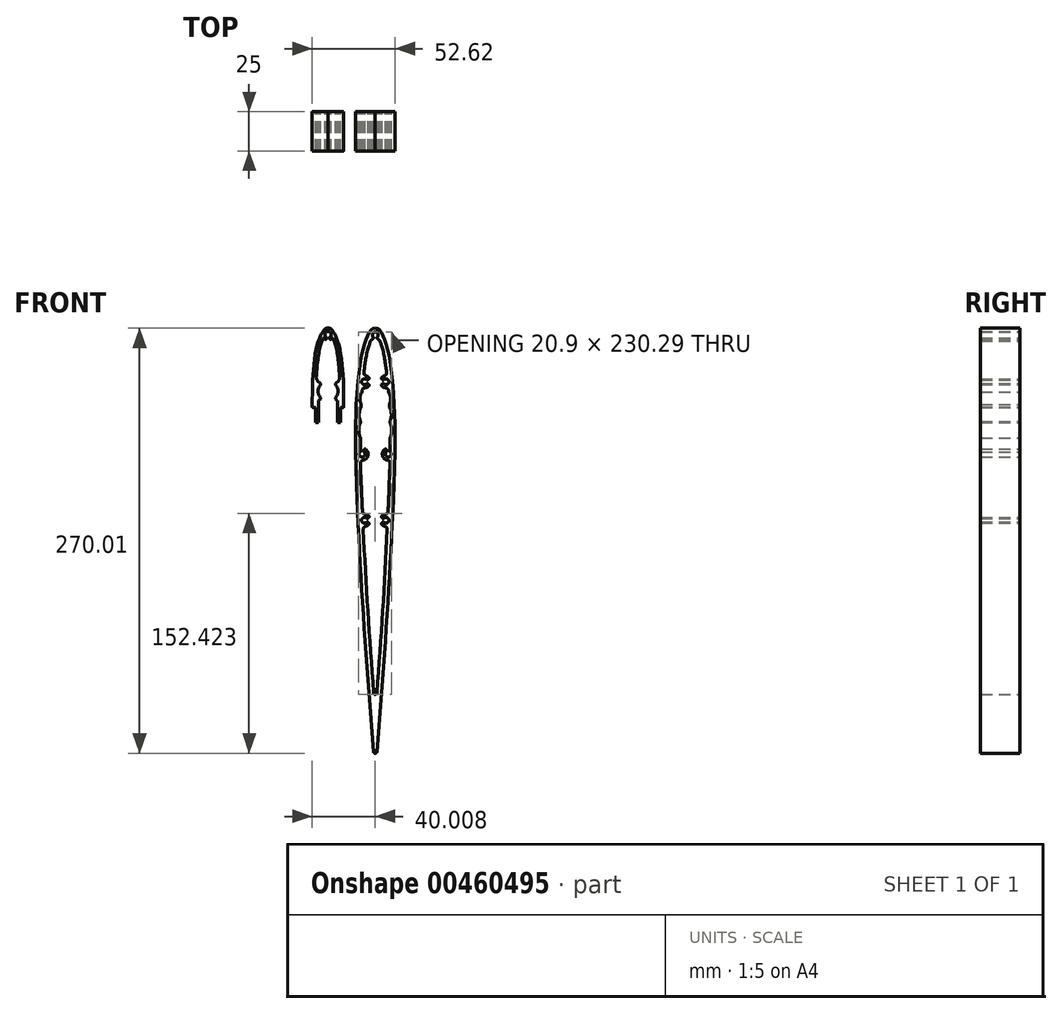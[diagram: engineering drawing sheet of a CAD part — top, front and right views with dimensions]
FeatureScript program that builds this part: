
annotation { "Feature Type Name" : "Feature", "Feature Type Description" : "" }
export const myFeature = defineFeature(function(context is Context, id is Id, definition is map)
    precondition{}
    {
        {
            var Q0;
            Q0=qCreatedBy(makeId("Front.planeOp"),FACE);
            var sketch = newSketch(context, id + "F0", { "sketchPlane" : qUnion([Q0])});
            skLineSegment(sketch, "E0", {"start": v(-26, 84.74) * mm, "end": v(-24.5, 84.74) * mm});
            skArc(sketch, "E1", {"start": v(-26.25, 85) * mm, "mid": v(-26.17, 84.82) * mm, "end": v(-26, 84.74) * mm});
            skFitSpline(sketch, "E2", {"points": [v(-26.25, 85) * mm, v(-26.24, 88.67) * mm, v(-26.08, 98.58) * mm, v(-25.1, 113) * mm, v(-22.87, 125.21) * mm, v(-20.9, 130.42) * mm, v(-19.33, 133.17) * mm, v(-17.9, 134.65) * mm, v(-16.79, 135) * mm, v(-16.24, 135) * mm]});
            skFitSpline(sketch, "E3", {"points": [v(-16.24, 135) * mm, v(-15.7, 135) * mm, v(-14.58, 134.65) * mm, v(-13.16, 133.17) * mm, v(-11.58, 130.42) * mm, v(-9.61, 125.21) * mm, v(-7.38, 113) * mm, v(-6.4, 98.58) * mm, v(-6.24, 88.67) * mm, v(-6.24, 85) * mm]});
            skArc(sketch, "E4", {"start": v(-6.49, 84.74) * mm, "mid": v(-6.3, 84.82) * mm, "end": v(-6.24, 85) * mm});
            skLineSegment(sketch, "E5", {"start": v(-7.99, 84.74) * mm, "end": v(-6.49, 84.74) * mm});
            skArc(sketch, "E6", {"start": v(-7.99, 84.74) * mm, "mid": v(-8.16, 84.67) * mm, "end": v(-8.24, 84.5) * mm});
            skLineSegment(sketch, "E7", {"start": v(-8.24, 84.5) * mm, "end": v(-8.24, 75) * mm});
            skArc(sketch, "E8", {"start": v(-10.24, 88.79) * mm, "mid": v(-10.27, 88.98) * mm, "end": v(-10.38, 89.14) * mm});
            skLineSegment(sketch, "E9", {"start": v(-11.41, 90.17) * mm, "end": v(-10.38, 89.14) * mm});
            skArc(sketch, "E10", {"start": v(-11.44, 90.85) * mm, "mid": v(-11.56, 90.5) * mm, "end": v(-11.41, 90.17) * mm});
            skArc(sketch, "E11", {"start": v(-11.44, 90.85) * mm, "mid": v(-9.9, 95) * mm, "end": v(-11.44, 99.15) * mm});
            skArc(sketch, "E12", {"start": v(-11.41, 99.83) * mm, "mid": v(-11.56, 99.5) * mm, "end": v(-11.44, 99.15) * mm});
            skLineSegment(sketch, "E13", {"start": v(-11.41, 99.83) * mm, "end": v(-9.68, 101.56) * mm});
            skArc(sketch, "E14", {"start": v(-9.68, 101.56) * mm, "mid": v(-9, 102.63) * mm, "end": v(-8.81, 103.89) * mm});
            skFitSpline(sketch, "E15", {"points": [v(-8.81, 103.89) * mm, v(-8.97, 106.15) * mm, v(-9.72, 114.71) * mm, v(-11.32, 123.38) * mm, v(-12.63, 127.4) * mm, v(-12.98, 128.32) * mm]});
            skArc(sketch, "E16", {"start": v(-12.98, 128.32) * mm, "mid": v(-13.34, 128.63) * mm, "end": v(-13.8, 128.5) * mm});
            skArc(sketch, "E17", {"start": v(-14.5, 127.97) * mm, "mid": v(-14.13, 128.21) * mm, "end": v(-13.8, 128.5) * mm});
            skArc(sketch, "E18", {"start": v(-15.24, 128.4) * mm, "mid": v(-15, 127.97) * mm, "end": v(-14.5, 127.97) * mm});
            skLineSegment(sketch, "E19", {"start": v(-15.24, 129) * mm, "end": v(-15.24, 128.4) * mm});
            skArc(sketch, "E20", {"start": v(-15.04, 129.4) * mm, "mid": v(-15.19, 129.22) * mm, "end": v(-15.24, 129) * mm});
            skArc(sketch, "E21", {"start": v(-15.04, 129.4) * mm, "mid": v(-16.24, 133) * mm, "end": v(-17.44, 129.4) * mm});
            skArc(sketch, "E22", {"start": v(-17.24, 129) * mm, "mid": v(-17.3, 129.22) * mm, "end": v(-17.44, 129.4) * mm});
            skLineSegment(sketch, "E23", {"start": v(-17.24, 128.4) * mm, "end": v(-17.24, 129) * mm});
            skArc(sketch, "E24", {"start": v(-18, 127.97) * mm, "mid": v(-17.5, 127.97) * mm, "end": v(-17.24, 128.4) * mm});
            skArc(sketch, "E25", {"start": v(-18.69, 128.5) * mm, "mid": v(-18.36, 128.21) * mm, "end": v(-18, 127.97) * mm});
            skArc(sketch, "E26", {"start": v(-18.69, 128.5) * mm, "mid": v(-19.15, 128.63) * mm, "end": v(-19.5, 128.32) * mm});
            skFitSpline(sketch, "E27", {"points": [v(-19.5, 128.32) * mm, v(-19.86, 127.4) * mm, v(-21.16, 123.38) * mm, v(-22.76, 114.71) * mm, v(-23.52, 106.15) * mm, v(-23.67, 103.89) * mm]});
            skArc(sketch, "E28", {"start": v(-23.67, 103.89) * mm, "mid": v(-23.49, 102.63) * mm, "end": v(-22.8, 101.56) * mm});
            skLineSegment(sketch, "E29", {"start": v(-22.8, 101.56) * mm, "end": v(-21.07, 99.83) * mm});
            skArc(sketch, "E30", {"start": v(-21.05, 99.15) * mm, "mid": v(-20.93, 99.5) * mm, "end": v(-21.07, 99.83) * mm});
            skArc(sketch, "E31", {"start": v(-21.05, 99.15) * mm, "mid": v(-22.6, 95) * mm, "end": v(-21.05, 90.85) * mm});
            skArc(sketch, "E32", {"start": v(-21.07, 90.17) * mm, "mid": v(-20.93, 90.5) * mm, "end": v(-21.05, 90.85) * mm});
            skLineSegment(sketch, "E33", {"start": v(-22.1, 89.14) * mm, "end": v(-21.07, 90.17) * mm});
            skArc(sketch, "E34", {"start": v(-22.1, 89.14) * mm, "mid": v(-22.2, 88.98) * mm, "end": v(-22.25, 88.79) * mm});
            skLineSegment(sketch, "E35", {"start": v(-24.25, 75) * mm, "end": v(-24.25, 84.5) * mm});
            skArc(sketch, "E36", {"start": v(-24.25, 84.5) * mm, "mid": v(-24.32, 84.67) * mm, "end": v(-24.5, 84.74) * mm});
            skLineSegment(sketch, "E37", {"start": v(-8.24, 75) * mm, "end": v(-10.24, 75) * mm});
            skLineSegment(sketch, "E38", {"start": v(-22.25, 88.79) * mm, "end": v(-22.25, 75) * mm});
            skLineSegment(sketch, "E39", {"start": v(-22.25, 75) * mm, "end": v(-24.25, 75) * mm});
            skLineSegment(sketch, "E40", {"start": v(-10.24, 75) * mm, "end": v(-10.24, 88.79) * mm});
            skArc(sketch, "E41", {"start": v(1.9, 35) * mm, "mid": v(5.19, -30.83) * mm, "end": v(9.73, -96.58) * mm});
            skFitSpline(sketch, "E42", {"points": [v(1.9, 35) * mm, v(1.67, 41.44) * mm, v(1.23, 54.34) * mm, v(1.24, 72.62) * mm, v(1.85, 89.82) * mm, v(2.95, 103.2) * mm, v(4.43, 113.85) * mm, v(5.71, 120.45) * mm, v(7.11, 125.63) * mm, v(8.23, 128.8) * mm, v(9.37, 131.23) * mm, v(10.3, 132.77) * mm, v(11.33, 133.95) * mm, v(12.42, 134.8) * mm, v(13.31, 134.93) * mm, v(13.76, 135) * mm]});
            skFitSpline(sketch, "E43", {"points": [v(25.63, 35) * mm, v(25.85, 41.44) * mm, v(26.29, 54.34) * mm, v(26.28, 72.62) * mm, v(25.66, 89.82) * mm, v(24.57, 103.2) * mm, v(23.09, 113.85) * mm, v(21.8, 120.45) * mm, v(20.4, 125.63) * mm, v(19.3, 128.8) * mm, v(18.15, 131.23) * mm, v(17.2, 132.77) * mm, v(16.18, 133.95) * mm, v(15.1, 134.8) * mm, v(14.2, 134.93) * mm, v(13.76, 135) * mm]});
            skArc(sketch, "E44", {"start": v(17.78, -96.58) * mm, "mid": v(22.33, -30.83) * mm, "end": v(25.63, 35) * mm});
            skLineSegment(sketch, "E45", {"start": v(14.84, -134) * mm, "end": v(17.78, -96.58) * mm});
            skLineSegment(sketch, "E46", {"start": v(12.68, -134) * mm, "end": v(9.73, -96.58) * mm});
            skArc(sketch, "E47", {"start": v(11.9, 127.93) * mm, "mid": v(12.51, 128.6) * mm, "end": v(12.32, 129.5) * mm});
            skArc(sketch, "E48", {"start": v(11.9, 127.93) * mm, "mid": v(11.17, 127.47) * mm, "end": v(10.7, 126.74) * mm});
            skFitSpline(sketch, "E49", {"points": [v(6.52, 106.91) * mm, v(6.59, 107.43) * mm, v(7.07, 111.18) * mm, v(8.03, 116.97) * mm, v(9.45, 123.07) * mm, v(10.41, 125.9) * mm, v(10.7, 126.74) * mm]});
            skArc(sketch, "E50", {"start": v(6.52, 106.91) * mm, "mid": v(6.84, 105.55) * mm, "end": v(7.98, 104.73) * mm});
            skArc(sketch, "E51", {"start": v(9.43, 103.98) * mm, "mid": v(8.75, 104.44) * mm, "end": v(7.98, 104.73) * mm});
            skArc(sketch, "E52", {"start": v(8.16, 102.44) * mm, "mid": v(9.56, 102.57) * mm, "end": v(9.43, 103.98) * mm});
            skArc(sketch, "E53", {"start": v(8.16, 102.44) * mm, "mid": v(5.1, 101) * mm, "end": v(8.16, 99.56) * mm});
            skArc(sketch, "E54", {"start": v(9.43, 98.02) * mm, "mid": v(9.56, 99.43) * mm, "end": v(8.16, 99.56) * mm});
            skArc(sketch, "E55", {"start": v(7.22, 97.14) * mm, "mid": v(8.4, 97.4) * mm, "end": v(9.43, 98.02) * mm});
            skArc(sketch, "E56", {"start": v(7.22, 97.14) * mm, "mid": v(5.94, 96.56) * mm, "end": v(5.36, 95.3) * mm});
            skLineSegment(sketch, "E57", {"start": v(5.28, 94.32) * mm, "end": v(5.36, 95.3) * mm});
            skArc(sketch, "E58", {"start": v(5.28, 94.32) * mm, "mid": v(4.02, 90.49) * mm, "end": v(4.8, 86.54) * mm});
            skLineSegment(sketch, "E59", {"start": v(4.72, 84.84) * mm, "end": v(4.8, 86.54) * mm});
            skArc(sketch, "E60", {"start": v(4.72, 84.84) * mm, "mid": v(3.54, 80.36) * mm, "end": v(4.4, 75.81) * mm});
            skLineSegment(sketch, "E61", {"start": v(4.4, 75.18) * mm, "end": v(4.4, 75.81) * mm});
            skArc(sketch, "E62", {"start": v(4.4, 75.18) * mm, "mid": v(3.3, 70.2) * mm, "end": v(4.27, 65.18) * mm});
            skLineSegment(sketch, "E63", {"start": v(4.31, 56.5) * mm, "end": v(4.27, 65.18) * mm});
            skArc(sketch, "E64", {"start": v(4.31, 56.5) * mm, "mid": v(5.37, 53.13) * mm, "end": v(6.65, 56.42) * mm});
            skArc(sketch, "E65", {"start": v(7.96, 57.93) * mm, "mid": v(6.55, 57.83) * mm, "end": v(6.65, 56.42) * mm});
            skArc(sketch, "E66", {"start": v(6.1, 51.19) * mm, "mid": v(9.16, 53.97) * mm, "end": v(7.96, 57.93) * mm});
            skArc(sketch, "E67", {"start": v(6.1, 51.19) * mm, "mid": v(4.9, 50.49) * mm, "end": v(4.44, 49.17) * mm});
            skLineSegment(sketch, "E68", {"start": v(4.89, 35.12) * mm, "end": v(4.44, 49.17) * mm});
            skArc(sketch, "E69", {"start": v(4.89, 35.12) * mm, "mid": v(5.23, 26.93) * mm, "end": v(5.6, 18.75) * mm});
            skArc(sketch, "E70", {"start": v(5.6, 18.75) * mm, "mid": v(6.13, 17.47) * mm, "end": v(7.37, 16.85) * mm});
            skArc(sketch, "E71", {"start": v(9.43, 15.98) * mm, "mid": v(8.46, 16.57) * mm, "end": v(7.37, 16.85) * mm});
            skArc(sketch, "E72", {"start": v(8.15, 14.44) * mm, "mid": v(9.56, 14.57) * mm, "end": v(9.43, 15.98) * mm});
            skArc(sketch, "E73", {"start": v(8.15, 14.44) * mm, "mid": v(5.09, 13) * mm, "end": v(8.15, 11.56) * mm});
            skArc(sketch, "E74", {"start": v(9.43, 10.02) * mm, "mid": v(9.56, 11.43) * mm, "end": v(8.15, 11.56) * mm});
            skArc(sketch, "E75", {"start": v(7.73, 9.2) * mm, "mid": v(8.63, 9.5) * mm, "end": v(9.43, 10.02) * mm});
            skArc(sketch, "E76", {"start": v(7.73, 9.2) * mm, "mid": v(6.55, 8.48) * mm, "end": v(6.14, 7.15) * mm});
            skArc(sketch, "E77", {"start": v(6.14, 7.15) * mm, "mid": v(9.04, -44.62) * mm, "end": v(12.73, -96.34) * mm});
            skLineSegment(sketch, "E78", {"start": v(12.76, -96.8) * mm, "end": v(12.73, -96.34) * mm});
            skArc(sketch, "E79", {"start": v(12.76, -96.8) * mm, "mid": v(13.76, -97.72) * mm, "end": v(14.76, -96.8) * mm});
            skLineSegment(sketch, "E80", {"start": v(14.76, -96.8) * mm, "end": v(14.8, -96.34) * mm});
            skArc(sketch, "E81", {"start": v(14.8, -96.34) * mm, "mid": v(18.47, -44.62) * mm, "end": v(21.38, 7.15) * mm});
            skArc(sketch, "E82", {"start": v(21.38, 7.15) * mm, "mid": v(20.96, 8.48) * mm, "end": v(19.78, 9.2) * mm});
            skArc(sketch, "E83", {"start": v(18.1, 10.02) * mm, "mid": v(18.89, 9.5) * mm, "end": v(19.78, 9.2) * mm});
            skArc(sketch, "E84", {"start": v(19.37, 11.56) * mm, "mid": v(17.96, 11.43) * mm, "end": v(18.1, 10.02) * mm});
            skArc(sketch, "E85", {"start": v(19.37, 11.56) * mm, "mid": v(22.43, 13) * mm, "end": v(19.37, 14.44) * mm});
            skArc(sketch, "E86", {"start": v(20.14, 16.85) * mm, "mid": v(19.05, 16.57) * mm, "end": v(18.1, 15.98) * mm});
            skArc(sketch, "E87", {"start": v(20.14, 16.85) * mm, "mid": v(21.39, 17.47) * mm, "end": v(21.93, 18.75) * mm});
            skArc(sketch, "E88", {"start": v(21.93, 18.75) * mm, "mid": v(22.29, 26.93) * mm, "end": v(22.63, 35.12) * mm});
            skLineSegment(sketch, "E89", {"start": v(22.63, 35.12) * mm, "end": v(23.08, 49.17) * mm});
            skArc(sketch, "E90", {"start": v(23.08, 49.17) * mm, "mid": v(22.62, 50.49) * mm, "end": v(21.42, 51.19) * mm});
            skArc(sketch, "E91", {"start": v(19.56, 57.93) * mm, "mid": v(18.35, 53.97) * mm, "end": v(21.42, 51.19) * mm});
            skArc(sketch, "E92", {"start": v(20.87, 56.42) * mm, "mid": v(20.97, 57.83) * mm, "end": v(19.56, 57.93) * mm});
            skArc(sketch, "E93", {"start": v(20.87, 56.42) * mm, "mid": v(22.15, 53.13) * mm, "end": v(23.2, 56.5) * mm});
            skLineSegment(sketch, "E94", {"start": v(23.2, 56.5) * mm, "end": v(23.25, 65.18) * mm});
            skArc(sketch, "E95", {"start": v(23.25, 65.18) * mm, "mid": v(24.2, 70.2) * mm, "end": v(23.12, 75.18) * mm});
            skArc(sketch, "E96", {"start": v(23.1, 75.81) * mm, "mid": v(23.98, 80.36) * mm, "end": v(22.8, 84.84) * mm});
            skLineSegment(sketch, "E97", {"start": v(22.8, 84.84) * mm, "end": v(22.71, 86.54) * mm});
            skArc(sketch, "E98", {"start": v(22.71, 86.54) * mm, "mid": v(23.5, 90.49) * mm, "end": v(22.23, 94.32) * mm});
            skLineSegment(sketch, "E99", {"start": v(22.23, 94.32) * mm, "end": v(22.16, 95.3) * mm});
            skArc(sketch, "E100", {"start": v(22.16, 95.3) * mm, "mid": v(21.57, 96.56) * mm, "end": v(20.3, 97.14) * mm});
            skArc(sketch, "E101", {"start": v(18.09, 98.02) * mm, "mid": v(19.12, 97.4) * mm, "end": v(20.3, 97.14) * mm});
            skArc(sketch, "E102", {"start": v(19.36, 99.56) * mm, "mid": v(17.95, 99.43) * mm, "end": v(18.09, 98.02) * mm});
            skArc(sketch, "E103", {"start": v(19.36, 99.56) * mm, "mid": v(22.42, 101) * mm, "end": v(19.36, 102.44) * mm});
            skArc(sketch, "E104", {"start": v(18.09, 103.98) * mm, "mid": v(17.95, 102.57) * mm, "end": v(19.36, 102.44) * mm});
            skArc(sketch, "E105", {"start": v(19.54, 104.73) * mm, "mid": v(18.77, 104.44) * mm, "end": v(18.09, 103.98) * mm});
            skArc(sketch, "E106", {"start": v(19.54, 104.73) * mm, "mid": v(20.67, 105.55) * mm, "end": v(21, 106.91) * mm});
            skFitSpline(sketch, "E107", {"points": [v(21, 106.91) * mm, v(20.93, 107.43) * mm, v(20.44, 111.18) * mm, v(19.49, 116.97) * mm, v(18.07, 123.07) * mm, v(17.1, 125.9) * mm, v(16.81, 126.74) * mm]});
            skArc(sketch, "E108", {"start": v(16.81, 126.74) * mm, "mid": v(16.35, 127.47) * mm, "end": v(15.62, 127.93) * mm});
            skArc(sketch, "E109", {"start": v(15.2, 129.5) * mm, "mid": v(15, 128.6) * mm, "end": v(15.62, 127.93) * mm});
            skArc(sketch, "E110", {"start": v(15.2, 129.5) * mm, "mid": v(13.76, 132.57) * mm, "end": v(12.32, 129.5) * mm});
            skArc(sketch, "E111", {"start": v(18.1, 15.98) * mm, "mid": v(17.96, 14.57) * mm, "end": v(19.37, 14.44) * mm});
            skArc(sketch, "E112", {"start": v(12.68, -134) * mm, "mid": v(13.76, -135) * mm, "end": v(14.84, -134) * mm});
            skLineSegment(sketch, "E113", {"start": v(23.12, 75.18) * mm, "end": v(23.1, 75.81) * mm});
            skSolve(sketch);
        }
        {
            var Q0;
            Q0=makeQuery(id+"F0.imprint","IMPRINT",FACE,{"disambiguationData":[TD([[makeQuery(id+"F0.imprint","IMPRINT",EDGE,{"derivedFrom":sQuery(id+"F0.wireOp",EDGE,"E41")}),1.0]])]});
            extrude(context, id + "F1", {"entities" : qUnion([Q0]), "depth" : 25 * mm});
        }
        {
            var Q0;
            Q0=makeQuery(id+"F0.imprint","IMPRINT",FACE,{"disambiguationData":[TD([[makeQuery(id+"F0.imprint","IMPRINT",EDGE,{"derivedFrom":sQuery(id+"F0.wireOp",EDGE,"E0")}),1.0]])]});
            extrude(context, id + "F2", {"entities" : qUnion([Q0]), "depth" : 25 * mm, "offsetDistance" : 25 * mm});
        }
    });
